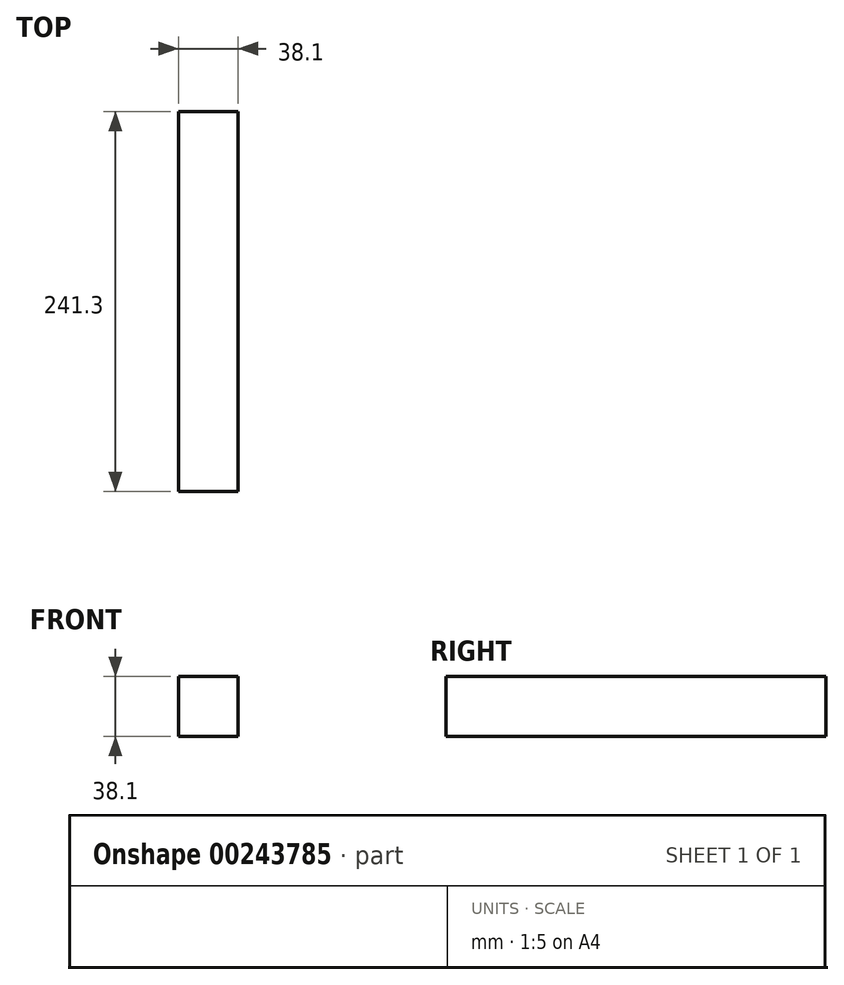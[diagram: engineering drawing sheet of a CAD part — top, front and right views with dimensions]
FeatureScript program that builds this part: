
annotation { "Feature Type Name" : "Feature", "Feature Type Description" : "" }
export const myFeature = defineFeature(function(context is Context, id is Id, definition is map)
    precondition{}
    {
        {
            var Q0;
            Q0=qCreatedBy(makeId("Front.planeOp"),FACE);
            var sketch = newSketch(context, id + "F0", { "sketchPlane" : qUnion([Q0])});
            skLineSegment(sketch, "E0.bottom", {"start": v(-38.1, 38.1) * mm, "end": v(0, 38.1) * mm});
            skLineSegment(sketch, "E0.top", {"start": v(-38.1, 0) * mm, "end": v(0, 0) * mm});
            skLineSegment(sketch, "E0.left", {"start": v(-38.1, 38.1) * mm, "end": v(-38.1, 0) * mm});
            skLineSegment(sketch, "E0.right", {"start": v(0, 38.1) * mm, "end": v(0, 0) * mm});
            skSolve(sketch);
        }
        {
            var Q0;
            Q0=makeQuery(id+"F0.imprint","IMPRINT",FACE,{"disambiguationData":[TD([[makeQuery(id+"F0.imprint","IMPRINT",EDGE,{"derivedFrom":sQuery(id+"F0.wireOp",EDGE,"E0.bottom")}),-1.0]])]});
            extrude(context, id + "F1", {"entities" : qUnion([Q0]), "depth" : 241.3 * mm});
        }
    });
